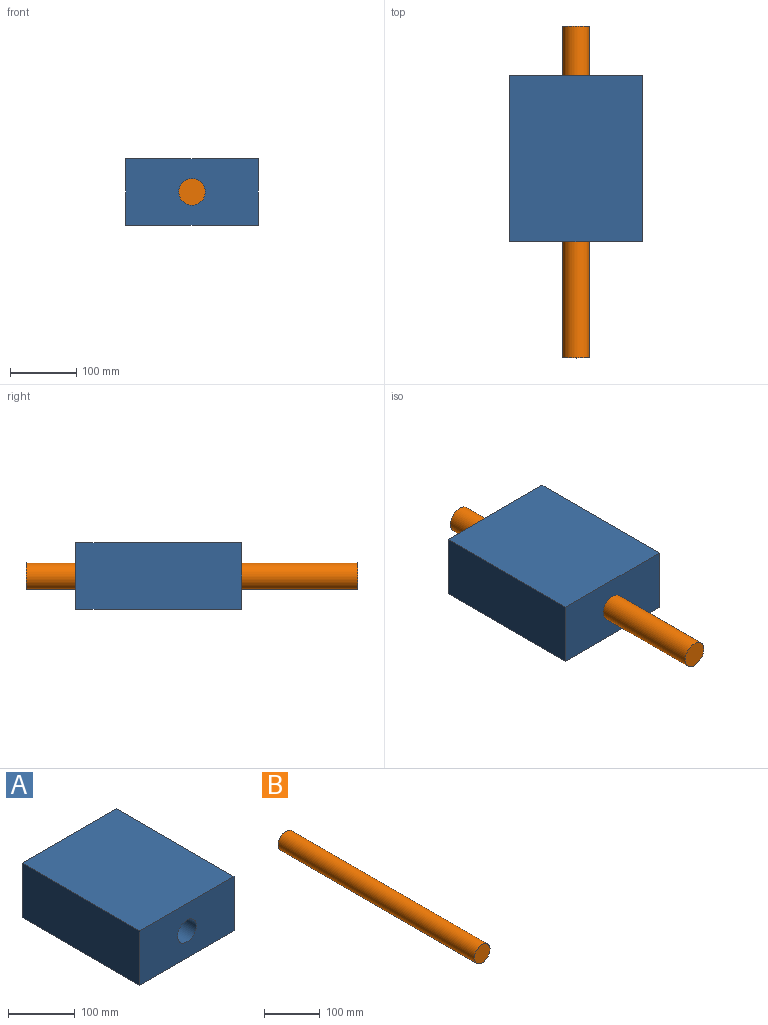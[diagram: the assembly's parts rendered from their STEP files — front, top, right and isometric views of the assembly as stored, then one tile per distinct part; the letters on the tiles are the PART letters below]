
ASSEMBLY  parts=2 mates=1
PART A: 7 faces, bbox 200x250x100 mm
  f0: plane 250x100mm, normal (-1,0,0), area 25000mm2, adj f1,f3,f4,f5
  f1: plane 250x200mm, normal (0,0,-1), area 50000mm2, adj f0,f2,f4,f5
  f2: plane 250x100mm, normal (1,0,0), area 25000mm2, adj f1,f3,f4,f5
  f3: plane 250x200mm, normal (0,0,1), area 50000mm2, adj f0,f2,f4,f5
  f4: plane 200x100mm, normal (0,-1,0), area 18743.4mm2, adj f0,f1,f2,f3,f6
  f5: plane 200x100mm, normal (0,1,0), area 18743.4mm2, adj f0,f1,f2,f3,f6
  f6: cylinder r=20mm len=250mm, axis (0,-1,0), area 31415.9mm2, adj f4,f5
PART B: 3 faces, bbox 40x500x40 mm
  f0: cylinder r=20mm len=500mm, axis (0,1,0), area 62831.9mm2, adj f1,f2
  f1: plane 40x40mm, normal (0,-1,0), area 1256.6mm2, adj f0
  f2: plane 40x40mm, normal (0,1,0), area 1256.6mm2, adj f0
PLACE A t=(232.23,194.63,90.82)mm fixed
PLACE B t=(332.23,269.75,140.82)mm
MATE slider B.f0 <-> A.f6  axis (0,1,0) through (332.23,19.75,140.82)mm
